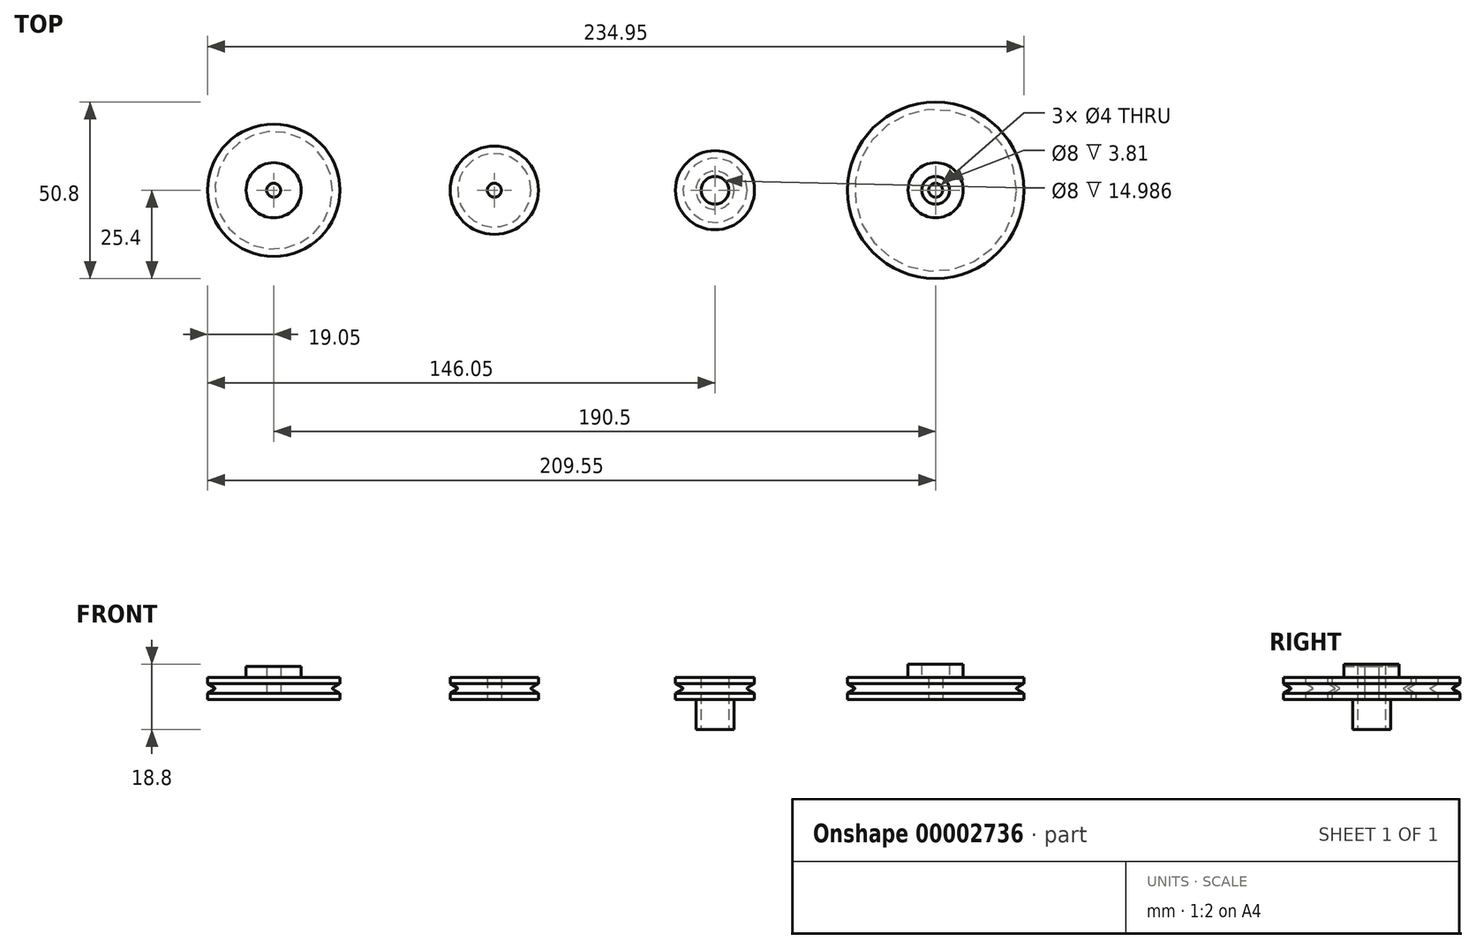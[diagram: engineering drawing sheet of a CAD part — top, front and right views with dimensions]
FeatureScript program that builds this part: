
annotation { "Feature Type Name" : "Feature", "Feature Type Description" : "" }
export const myFeature = defineFeature(function(context is Context, id is Id, definition is map)
    precondition{}
    {
        {
            var Q0;
            Q0=qCreatedBy(makeId("Top.planeOp"),FACE);
            var sketch = newSketch(context, id + "F0", { "sketchPlane" : qUnion([Q0])});
            skCircle(sketch, "E0", {"center": v(0, 0) * mm, "radius": 11.37 * mm});
            skCircle(sketch, "E1", {"center": v(63.5, 0) * mm, "radius": 25.4 * mm});
            skCircle(sketch, "E2", {"center": v(0, 0) * mm, "radius": 4 * mm});
            skCircle(sketch, "E3", {"center": v(63.5, 0) * mm, "radius": 2 * mm});
            skCircle(sketch, "E4", {"center": v(-63.5, 0) * mm, "radius": 12.7 * mm});
            skCircle(sketch, "E5", {"center": v(-127, 0) * mm, "radius": 19.05 * mm});
            skCircle(sketch, "E6", {"center": v(-127, 0) * mm, "radius": 2 * mm});
            skCircle(sketch, "E7", {"center": v(-63.5, 0) * mm, "radius": 2 * mm});
            skSolve(sketch);
        }
        {
            var Q0;
            {Q0=qUnion([makeQuery(id+"F0.imprint","IMPRINT",FACE,{"disambiguationData":[TD([[makeQuery(id+"F0.imprint","IMPRINT",EDGE,{"derivedFrom":sQuery(id+"F0.wireOp",EDGE,"E0")}),1.0]])]}),makeQuery(id+"F0.imprint","IMPRINT",FACE,{"disambiguationData":[TD([[makeQuery(id+"F0.imprint","IMPRINT",EDGE,{"derivedFrom":sQuery(id+"F0.wireOp",EDGE,"E1")}),1.0]])]}),makeQuery(id+"F0.imprint","IMPRINT",FACE,{"disambiguationData":[TD([[makeQuery(id+"F0.imprint","IMPRINT",EDGE,{"derivedFrom":sQuery(id+"F0.wireOp",EDGE,"E4")}),1.0]])]}),makeQuery(id+"F0.imprint","IMPRINT",FACE,{"disambiguationData":[TD([[makeQuery(id+"F0.imprint","IMPRINT",EDGE,{"derivedFrom":sQuery(id+"F0.wireOp",EDGE,"E5")}),1.0]])]})]);}
            extrude(context, id + "F1", {"entities" : qUnion([Q0]), "endBound" : BoundingType.SYMMETRIC, "depth" : 6.35 * mm});
        }
        {
            var Q0;
            Q0=qCreatedBy(makeId("Front.planeOp"),FACE);
            var sketch = newSketch(context, id + "F2", { "sketchPlane" : qUnion([Q0])});
            skLineSegment(sketch, "E8", {"start": v(63.5, 0) * mm, "end": v(63.5, 7.06) * mm, "construction": true});
            skLineSegment(sketch, "E9", {"start": v(0, 0) * mm, "end": v(0, 7.2) * mm, "construction": true});
            skLineSegment(sketch, "E10", {"start": v(86.94, 0.26) * mm, "end": v(88.9, 1.4) * mm});
            skLineSegment(sketch, "E11", {"start": v(86.94, -0.26) * mm, "end": v(88.9, -1.4) * mm});
            skLineSegment(sketch, "E12", {"start": v(9.4, 0.26) * mm, "end": v(11.37, 1.4) * mm});
            skLineSegment(sketch, "E13", {"start": v(9.4, -0.26) * mm, "end": v(11.37, -1.4) * mm});
            skLineSegment(sketch, "E14", {"start": v(9.53, 0) * mm, "end": v(9.53, 6.1) * mm, "construction": true});
            skLineSegment(sketch, "E15", {"start": v(0, 1.4) * mm, "end": v(122.96, 1.4) * mm, "construction": true});
            skLineSegment(sketch, "E16", {"start": v(0, 0) * mm, "end": v(17.93, 0) * mm, "construction": true});
            skLineSegment(sketch, "E17", {"start": v(11.37, 1.4) * mm, "end": v(11.37, -1.4) * mm});
            skLineSegment(sketch, "E18", {"start": v(88.9, 1.4) * mm, "end": v(88.9, -1.4) * mm});
            skPoint(sketch, "E19.visualSharp", {"position": v(86.48, 0) * mm});
            skArc(sketch, "E19.filletArc", {"start": v(86.94, 0.26) * mm, "mid": v(86.79, 0) * mm, "end": v(86.94, -0.26) * mm});
            skPoint(sketch, "E20.visualSharp", {"position": v(8.95, 0) * mm});
            skArc(sketch, "E20.filletArc", {"start": v(9.4, 0.26) * mm, "mid": v(9.25, 0) * mm, "end": v(9.4, -0.26) * mm});
            skLineSegment(sketch, "E21", {"start": v(-127, 0) * mm, "end": v(-127, 8.35) * mm, "construction": true});
            skLineSegment(sketch, "E22", {"start": v(-63.5, 0) * mm, "end": v(-63.5, 7.25) * mm, "construction": true});
            skLineSegment(sketch, "E23", {"start": v(0, 1.4) * mm, "end": v(-151.9, 1.4) * mm, "construction": true});
            skLineSegment(sketch, "E24", {"start": v(-50.8, -3.26) * mm, "end": v(-50.8, 3.38) * mm, "construction": true});
            skLineSegment(sketch, "E25", {"start": v(-107.95, -3.17) * mm, "end": v(-107.95, 3.38) * mm, "construction": true});
            skLineSegment(sketch, "E26", {"start": v(-50.8, 1.4) * mm, "end": v(-52.76, 0.26) * mm});
            skLineSegment(sketch, "E27", {"start": v(-107.95, 1.4) * mm, "end": v(-109.91, 0.26) * mm});
            skLineSegment(sketch, "E28.0.MirrorCS", {"start": v(-107.95, -1.4) * mm, "end": v(-109.91, -0.26) * mm});
            skLineSegment(sketch, "E29.0.MirrorCS", {"start": v(-50.8, -1.4) * mm, "end": v(-52.76, -0.26) * mm});
            skLineSegment(sketch, "E30", {"start": v(-107.95, 1.4) * mm, "end": v(-107.95, -1.4) * mm});
            skLineSegment(sketch, "E31", {"start": v(-50.8, 1.4) * mm, "end": v(-50.8, -1.4) * mm});
            skPoint(sketch, "E32.visualSharp", {"position": v(-53.22, 0) * mm});
            skArc(sketch, "E32.filletArc", {"start": v(-52.76, 0.26) * mm, "mid": v(-52.91, 0) * mm, "end": v(-52.76, -0.26) * mm});
            skPoint(sketch, "E33.visualSharp", {"position": v(-110.37, 0) * mm});
            skArc(sketch, "E33.filletArc", {"start": v(-109.91, 0.26) * mm, "mid": v(-110.06, 0) * mm, "end": v(-109.91, -0.26) * mm});
            skSolve(sketch);
        }
        {
            var Q0;
            Q0=makeQuery(id+"F2.imprint","IMPRINT",FACE,{"disambiguationData":[TD([[makeQuery(id+"F2.imprint","IMPRINT",EDGE,{"derivedFrom":sQuery(id+"F2.wireOp",EDGE,"E12")}),-1.0]])]});
            var Q1;
            Q1=sQuery(id+"F2.wireOp",EDGE,"E9");
            revolve(context, id + "F3", {"operationType" : NewBodyOperationType.REMOVE, "entities" : qUnion([Q0]), "axis" : qUnion([Q1]), "revolveType" : RevolveType.FULL, "oppositeDirection" : true});
        }
        {
            var Q0;
            Q0=makeQuery(id+"F2.imprint","IMPRINT",FACE,{"disambiguationData":[TD([[makeQuery(id+"F2.imprint","IMPRINT",EDGE,{"derivedFrom":sQuery(id+"F2.wireOp",EDGE,"E10")}),-1.0]])]});
            var Q1;
            Q1=sQuery(id+"F2.wireOp",EDGE,"E8");
            revolve(context, id + "F4", {"operationType" : NewBodyOperationType.REMOVE, "entities" : qUnion([Q0]), "axis" : qUnion([Q1]), "revolveType" : RevolveType.FULL, "oppositeDirection" : true});
        }
        {
            var Q0;
            Q0=makeQuery(id+"F1.opExtrude","CAP_FACE",FACE,{"disambiguationData":[OSD([sQuery(id+"F0.wireOp",EDGE,"E0"),sQuery(id+"F0.wireOp",EDGE,"E2")])],"isStart":false});
            var sketch = newSketch(context, id + "F5", { "sketchPlane" : qUnion([Q0])});
            skCircle(sketch, "E34", {"center": v(0, 0) * mm, "radius": 7.94 * mm});
            skCircle(sketch, "E35", {"center": v(63.5, 0) * mm, "radius": 7.94 * mm});
            skCircle(sketch, "E36", {"center": v(0, 0) * mm, "radius": 4 * mm});
            skCircle(sketch, "E37", {"center": v(63.5, 0) * mm, "radius": 4 * mm});
            skSolve(sketch);
        }
        {
            var Q0;
            Q0=makeQuery(id+"F5.imprint","IMPRINT",FACE,{"disambiguationData":[TD([[makeQuery(id+"F5.imprint","IMPRINT",EDGE,{"derivedFrom":sQuery(id+"F5.wireOp",EDGE,"E35")}),1.0]])]});
            extrude(context, id + "F6", {"entities" : qUnion([Q0]), "operationType" : NewBodyOperationType.ADD, "depth" : 3.8 * mm});
        }
        {
            var Q0;
            Q0=makeQuery(id+"F1.opExtrude","CAP_FACE",FACE,{"disambiguationData":[OSD([sQuery(id+"F0.wireOp",EDGE,"E0"),sQuery(id+"F0.wireOp",EDGE,"E2")])],"isStart":true});
            var sketch = newSketch(context, id + "F7", { "sketchPlane" : qUnion([Q0])});
            skCircle(sketch, "E38", {"center": v(0, 0) * mm, "radius": 5.5 * mm});
            skCircle(sketch, "E39", {"center": v(0, 0) * mm, "radius": 4 * mm});
            skSolve(sketch);
        }
        {
            var Q0;
            Q0=makeQuery(id+"F7.imprint","IMPRINT",FACE,{"disambiguationData":[TD([[makeQuery(id+"F7.imprint","IMPRINT",EDGE,{"derivedFrom":sQuery(id+"F7.wireOp",EDGE,"E38")}),1.0]])]});
            extrude(context, id + "F8", {"entities" : qUnion([Q0]), "operationType" : NewBodyOperationType.ADD, "depth" : 8.64 * mm});
        }
        {
            var Q0;
            Q0=makeQuery(id+"F2.imprint","IMPRINT",FACE,{"disambiguationData":[TD([[makeQuery(id+"F2.imprint","IMPRINT",EDGE,{"derivedFrom":sQuery(id+"F2.wireOp",EDGE,"E27")}),1.0]])]});
            var Q1;
            Q1=sQuery(id+"F2.wireOp",EDGE,"E21");
            revolve(context, id + "F9", {"operationType" : NewBodyOperationType.REMOVE, "entities" : qUnion([Q0]), "axis" : qUnion([Q1]), "revolveType" : RevolveType.FULL, "oppositeDirection" : true});
        }
        {
            var Q0;
            Q0=makeQuery(id+"F2.imprint","IMPRINT",FACE,{"disambiguationData":[TD([[makeQuery(id+"F2.imprint","IMPRINT",EDGE,{"derivedFrom":sQuery(id+"F2.wireOp",EDGE,"E26")}),1.0]])]});
            var Q1;
            Q1=sQuery(id+"F2.wireOp",EDGE,"E22");
            revolve(context, id + "F10", {"operationType" : NewBodyOperationType.REMOVE, "entities" : qUnion([Q0]), "axis" : qUnion([Q1]), "revolveType" : RevolveType.FULL, "oppositeDirection" : true});
        }
        {
            var Q0;
            Q0=qCreatedBy(makeId("Right.planeOp"),FACE);
            var sketch = newSketch(context, id + "F11", { "sketchPlane" : qUnion([Q0])});
            skLineSegment(sketch, "E40", {"start": v(-7.94, 6.97) * mm, "end": v(-7.94, 3.13) * mm, "construction": true});
            skCircle(sketch, "E41", {"center": v(0, 5.4) * mm, "radius": 1.13 * mm});
            skSolve(sketch);
        }
        {
            var Q0;
            Q0=makeQuery(id+"F11.imprint","IMPRINT",FACE,{"disambiguationData":[TD([[makeQuery(id+"F11.imprint","IMPRINT",EDGE,{"derivedFrom":sQuery(id+"F11.wireOp",EDGE,"E41")}),1.0]])]});
            extrude(context, id + "F12", {"entities" : qUnion([Q0]), "operationType" : NewBodyOperationType.REMOVE, "oppositeDirection" : true, "depth" : 12.7 * mm});
        }
        {
            var Q0;
            Q0=makeQuery(id+"F1.opExtrude","CAP_FACE",FACE,{"disambiguationData":[OSD([sQuery(id+"F0.wireOp",EDGE,"E5"),sQuery(id+"F0.wireOp",EDGE,"E6")])],"isStart":false});
            var sketch = newSketch(context, id + "F13", { "sketchPlane" : qUnion([Q0])});
            skCircle(sketch, "E42", {"center": v(-127, 0) * mm, "radius": 7.94 * mm});
            skSolve(sketch);
        }
        {
            var Q0;
            Q0=makeQuery(id+"F13.imprint","IMPRINT",FACE,{"disambiguationData":[TD([[makeQuery(id+"F13.imprint","IMPRINT",EDGE,{"derivedFrom":sQuery(id+"F13.wireOp",EDGE,"E42")}),1.0]])]});
            extrude(context, id + "F14", {"entities" : qUnion([Q0]), "operationType" : NewBodyOperationType.ADD, "depth" : 3.17 * mm});
        }
    });
